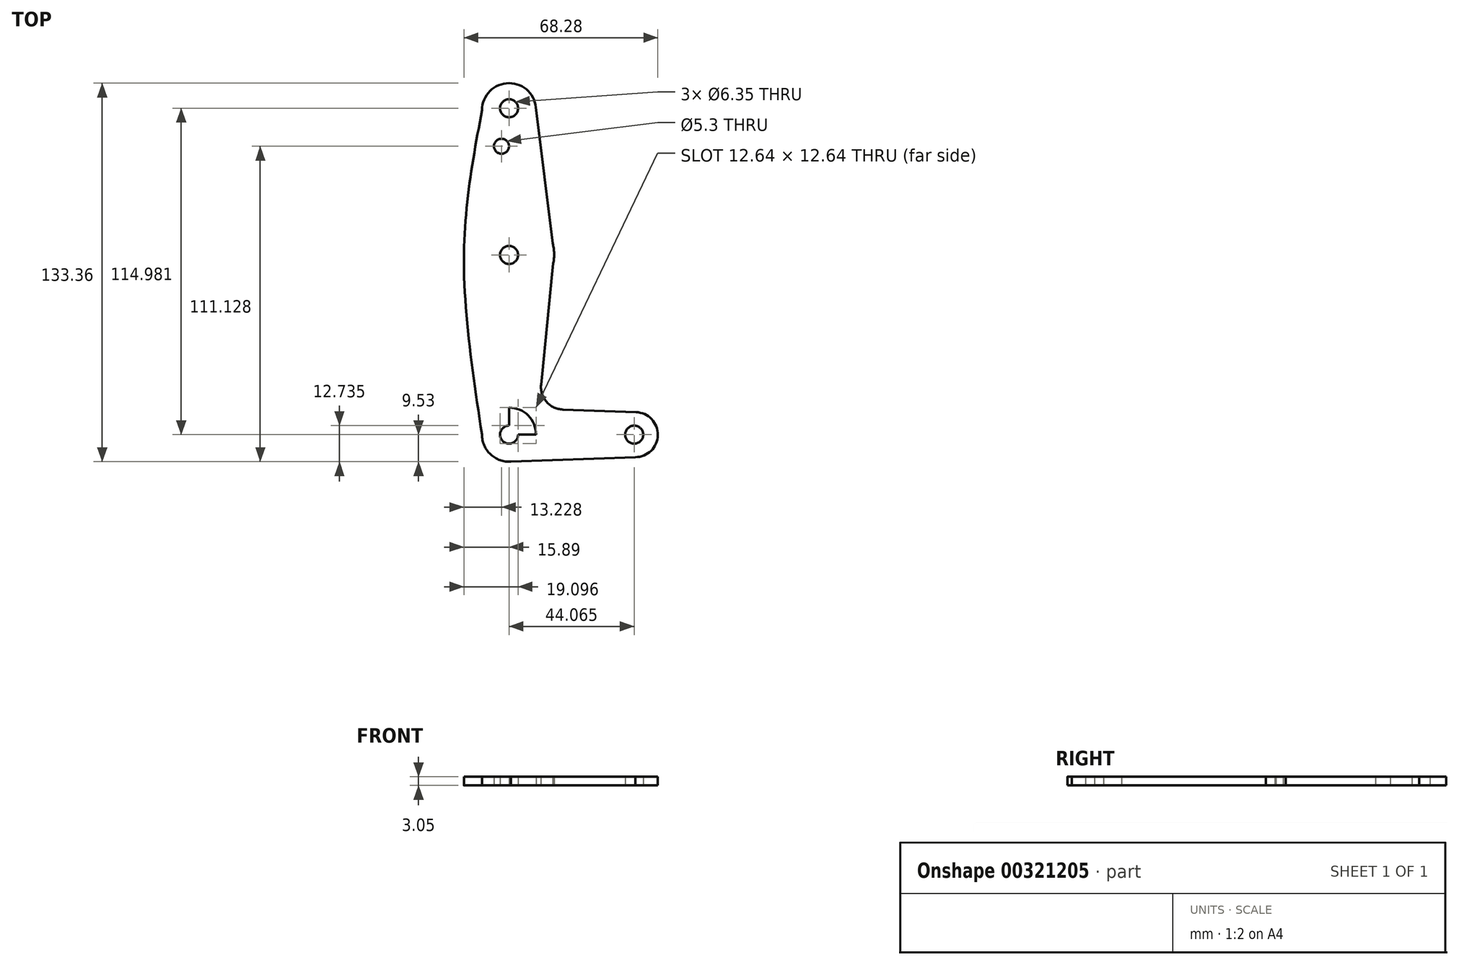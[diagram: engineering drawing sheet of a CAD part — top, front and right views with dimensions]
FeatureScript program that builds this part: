
annotation { "Feature Type Name" : "Feature", "Feature Type Description" : "" }
export const myFeature = defineFeature(function(context is Context, id is Id, definition is map)
    precondition{}
    {
        {
            var Q0;
            Q0=qCreatedBy(makeId("Top.planeOp"),FACE);
            var sketch = newSketch(context, id + "F0", { "sketchPlane" : qUnion([Q0])});
            skCircle(sketch, "E0", {"center": v(0, 0) * mm, "radius": 9.53 * mm});
            skLineSegment(sketch, "E1", {"start": v(0, 0) * mm, "end": v(44.45, 0) * mm});
            skCircle(sketch, "E2", {"center": v(44.45, 0) * mm, "radius": 7.94 * mm});
            skLineSegment(sketch, "E3", {"start": v(0, 0) * mm, "end": v(0, 63.5) * mm});
            skCircle(sketch, "E4", {"center": v(0, 63.5) * mm, "radius": 15.88 * mm});
            skLineSegment(sketch, "E5", {"start": v(0, 0) * mm, "end": v(0, 114.3) * mm});
            skCircle(sketch, "E6", {"center": v(0, 114.3) * mm, "radius": 9.52 * mm});
            skFitSpline(sketch, "E7", {"points": [v(-9.53, 114.3) * mm, v(-15.88, 63.5) * mm, v(-9.53, 0) * mm], "startDerivative": vector(-19.46, -104.48) * mm, "endDerivative": vector(18.76, -123.77) * mm});
            skFitSpline(sketch, "E8", {"points": [v(0, -9.53) * mm, v(44.45, -7.94) * mm], "startDerivative": vector(44.45, 1.59) * mm, "endDerivative": vector(44.45, 1.59) * mm});
            skLineSegment(sketch, "E9", {"start": v(0, 9.53) * mm, "end": v(0, 7.95) * mm});
            skLineSegment(sketch, "E10", {"start": v(9.53, 0) * mm, "end": v(7.95, 0) * mm});
            skArc(sketch, "E11", {"start": v(0, 9.53) * mm, "mid": v(-6.74, -6.74) * mm, "end": v(9.53, 0) * mm});
            skArc(sketch, "E12", {"start": v(0, -9.53) * mm, "mid": v(6.74, 6.74) * mm, "end": v(-9.53, 0) * mm});
            skLineSegment(sketch, "E13", {"start": v(9.52, 114.3) * mm, "end": v(15.88, 63.5) * mm});
            skLineSegment(sketch, "E14", {"start": v(15.88, 63.5) * mm, "end": v(11.28, 17.59) * mm});
            skLineSegment(sketch, "E15", {"start": v(18.91, 8.85) * mm, "end": v(44.73, 7.93) * mm});
            skArc(sketch, "E16.filletArc", {"start": v(11.28, 17.59) * mm, "mid": v(13.2, 11.57) * mm, "end": v(18.91, 8.85) * mm});
            skSolve(sketch);
        }
        {
            var Q0;
            Q0=qSketchRegion(id+"F0",true);
            var Q1;
            {var subQ3=sQuery(id+"F0.wireOp",EDGE,"E9");Q1=makeQuery(id+"F0.imprint","IMPRINT",FACE,{"disambiguationData":[TD([[makeQuery(id+"F0.imprint","IMPRINT",EDGE,{"derivedFrom":subQ3}),1.0]])]});}
            extrude(context, id + "F1", {"entities" : qUnion([Q0, Q1]), "depth" : 3.05 * mm});
        }
        {
            var Q0;
            Q0=qCreatedBy(makeId("Top.planeOp"),FACE);
            var sketch = newSketch(context, id + "F2", { "sketchPlane" : qUnion([Q0])});
            skCircle(sketch, "E17", {"center": v(0, 0) * mm, "radius": 3.18 * mm});
            skCircle(sketch, "E18", {"center": v(44.06, 0) * mm, "radius": 3.18 * mm});
            skCircle(sketch, "E19", {"center": v(0, 63.32) * mm, "radius": 3.17 * mm});
            skCircle(sketch, "E20", {"center": v(0, 114.98) * mm, "radius": 3.18 * mm});
            skCircle(sketch, "E21", {"center": v(-2.66, 101.6) * mm, "radius": 2.65 * mm});
            skSolve(sketch);
        }
        {
            var Q0;
            Q0=qSketchRegion(id+"F2",true);
            extrude(context, id + "F3", {"entities" : qUnion([Q0]), "operationType" : NewBodyOperationType.REMOVE, "depth" : 25.4 * mm});
        }
    });
